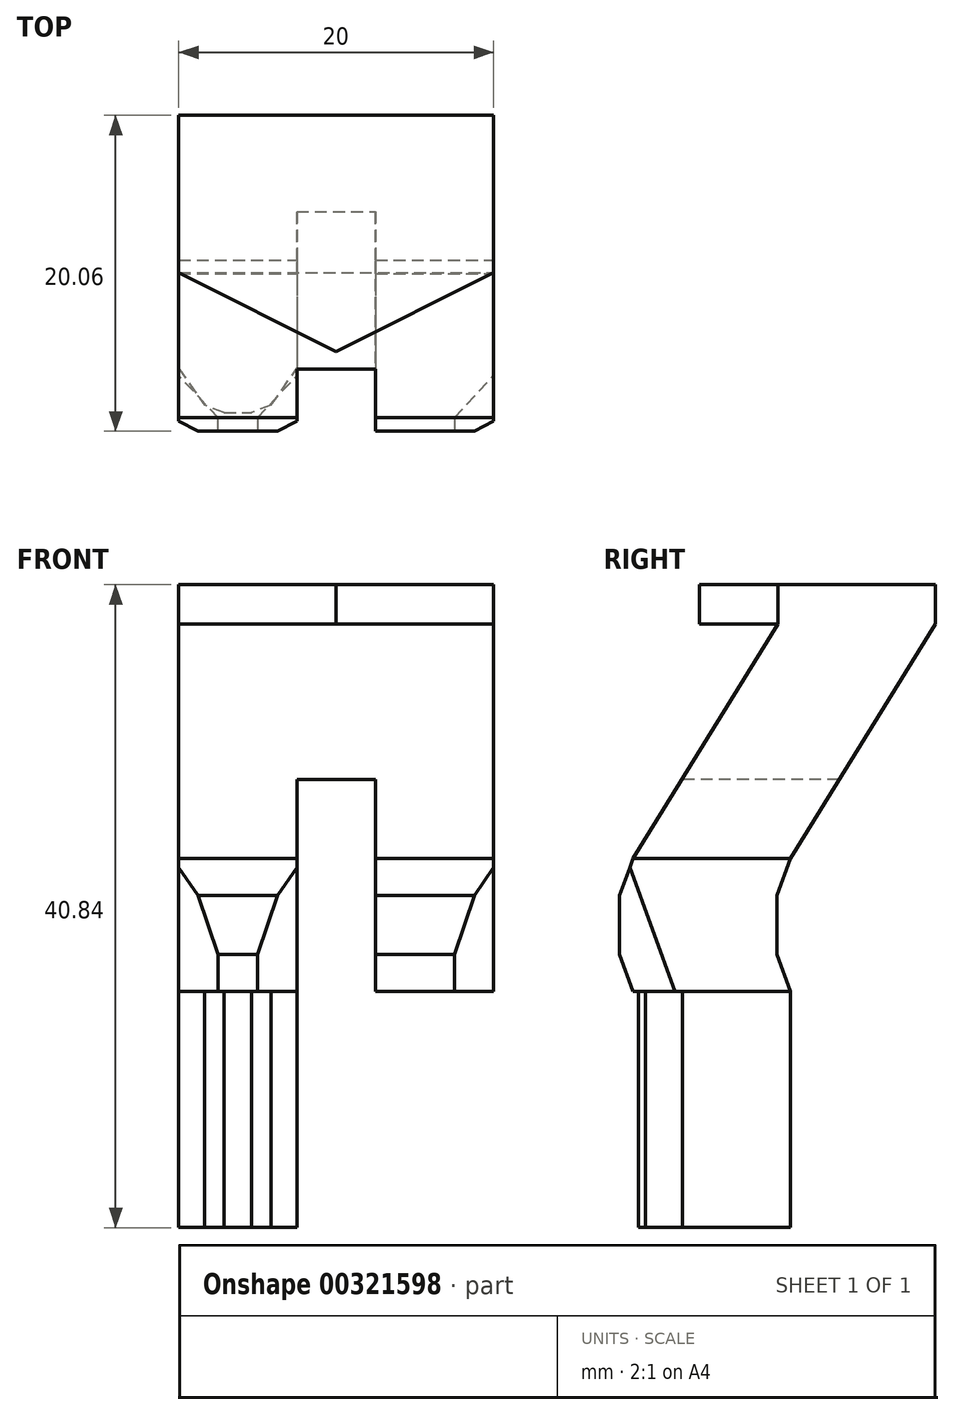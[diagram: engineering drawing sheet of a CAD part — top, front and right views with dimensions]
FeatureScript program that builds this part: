
annotation { "Feature Type Name" : "Feature", "Feature Type Description" : "" }
export const myFeature = defineFeature(function(context is Context, id is Id, definition is map)
    precondition{}
    {
        {
            var Q0;
            Q0=qCreatedBy(makeId("Top.planeOp"),FACE);
            var sketch = newSketch(context, id + "F0", { "sketchPlane" : qUnion([Q0])});
            skLineSegment(sketch, "E0", {"start": v(0, 0) * mm, "end": v(10, 0) * mm});
            skLineSegment(sketch, "E1", {"start": v(0, 0) * mm, "end": v(-10, 0) * mm});
            skLineSegment(sketch, "E2", {"start": v(-10, 0) * mm, "end": v(-10, -10) * mm});
            skLineSegment(sketch, "E3", {"start": v(10, 0) * mm, "end": v(10, -10) * mm});
            skLineSegment(sketch, "E4", {"start": v(0, 0) * mm, "end": v(0, -15) * mm});
            skLineSegment(sketch, "E5", {"start": v(-10, -10) * mm, "end": v(0, -15) * mm});
            skLineSegment(sketch, "E6", {"start": v(10, -10) * mm, "end": v(0, -15) * mm});
            skSolve(sketch);
        }
        {
            var Q0;
            Q0=makeQuery(id+"F0.imprint","IMPRINT",FACE,{"disambiguationData":[TD([[makeQuery(id+"F0.imprint","IMPRINT",EDGE,{"derivedFrom":sQuery(id+"F0.wireOp",EDGE,"E1")}),1.0]])]});
            var Q1;
            Q1=makeQuery(id+"F0.imprint","IMPRINT",FACE,{"disambiguationData":[TD([[makeQuery(id+"F0.imprint","IMPRINT",EDGE,{"derivedFrom":sQuery(id+"F0.wireOp",EDGE,"E0")}),-1.0]])]});
            extrude(context, id + "F1", {"entities" : qUnion([Q0, Q1]), "depth" : 2.5 * mm});
        }
        {
            var Q0;
            Q0=makeQuery(id+"F1.opExtrude","SWEPT_FACE",FACE,{"disambiguationData":[OSD([sQuery(id+"F0.wireOp",EDGE,"E3")])]});
            var sketch = newSketch(context, id + "F2", { "sketchPlane" : qUnion([Q0])});
            skLineSegment(sketch, "E7", {"start": v(-10, 0) * mm, "end": v(-19.2, -14.89) * mm});
            skLineSegment(sketch, "E8", {"start": v(-19.2, -14.89) * mm, "end": v(-9.2, -14.89) * mm});
            skLineSegment(sketch, "E9", {"start": v(0, 0) * mm, "end": v(-9.2, -14.89) * mm});
            skSolve(sketch);
        }
        {
            var Q0;
            Q0=makeQuery(id+"F2.imprint","IMPRINT",FACE,{"disambiguationData":[TD([[makeQuery(id+"F2.imprint","IMPRINT",EDGE,{"derivedFrom":sQuery(id+"F2.wireOp",EDGE,"E7")}),1.0]])]});
            extrude(context, id + "F3", {"entities" : qUnion([Q0]), "operationType" : NewBodyOperationType.ADD, "oppositeDirection" : true, "depth" : 20 * mm});
        }
        {
            var Q0;
            Q0=makeQuery(id+"F3.opExtrude","SWEPT_FACE",FACE,{"disambiguationData":[OSD([sQuery(id+"F2.wireOp",EDGE,"E8")])]});
            var sketch = newSketch(context, id + "F4", { "sketchPlane" : qUnion([Q0])});
            skLineSegment(sketch, "E10", {"start": v(-10, 9.2) * mm, "end": v(-2.5, 9.2) * mm});
            skLineSegment(sketch, "E11", {"start": v(10, 9.2) * mm, "end": v(2.5, 9.2) * mm});
            skLineSegment(sketch, "E12", {"start": v(-2.5, 9.2) * mm, "end": v(-2.5, 0) * mm});
            skLineSegment(sketch, "E13.bottom", {"start": v(-2.5, 0) * mm, "end": v(2.5, 0) * mm});
            skLineSegment(sketch, "E13.top", {"start": v(-2.5, 19.2) * mm, "end": v(2.5, 19.2) * mm});
            skLineSegment(sketch, "E13.left", {"start": v(-2.5, 0) * mm, "end": v(-2.5, 19.2) * mm});
            skLineSegment(sketch, "E13.right", {"start": v(2.5, 0) * mm, "end": v(2.5, 19.2) * mm});
            skSolve(sketch);
        }
        {
            var Q0;
            {var subQ0=sQuery(id+"F4.wireOp",EDGE,"E13.top");Q0=makeQuery(id+"F4.imprint","IMPRINT",FACE,{"disambiguationData":[TD([[makeQuery(id+"F4.imprint","IMPRINT",EDGE,{"derivedFrom":subQ0}),-1.0]])]});}
            var Q1;
            {var subQ0=sQuery(id+"F4.wireOp",EDGE,"E13.bottom");Q1=makeQuery(id+"F4.imprint","IMPRINT",FACE,{"disambiguationData":[TD([[makeQuery(id+"F4.imprint","IMPRINT",EDGE,{"derivedFrom":subQ0}),1.0]])]});}
            extrude(context, id + "F5", {"entities" : qUnion([Q0, Q1]), "operationType" : NewBodyOperationType.REMOVE, "oppositeDirection" : true, "depth" : 5 * mm});
        }
        {
            var Q0;
            {var subQ0=sQuery(id+"F0.wireOp",EDGE,"E3");Q0=makeQuery(id+"F3.boolean.opBoolean","MERGE",FACE,{"derivedFrom":[makeQuery(id+"F1.opExtrude","SWEPT_FACE",FACE,{"disambiguationData":[OSD([subQ0])]}),makeQuery(id+"F3.opExtrude","CAP_FACE",FACE,{"disambiguationData":[OSD([subQ0,sQuery(id+"F2.wireOp",EDGE,"E7"),sQuery(id+"F2.wireOp",EDGE,"E8"),sQuery(id+"F2.wireOp",EDGE,"E9")])],"isStart":true})]});}
            var sketch = newSketch(context, id + "F6", { "sketchPlane" : qUnion([Q0])});
            skLineSegment(sketch, "E14", {"start": v(-19.2, -14.89) * mm, "end": v(-20.06, -17.24) * mm});
            skLineSegment(sketch, "E15", {"start": v(-9.2, -14.89) * mm, "end": v(-10.06, -17.24) * mm});
            skLineSegment(sketch, "E16", {"start": v(-20.06, -17.24) * mm, "end": v(-20.06, -20.99) * mm});
            skLineSegment(sketch, "E17", {"start": v(-10.06, -17.24) * mm, "end": v(-10.06, -20.99) * mm});
            skLineSegment(sketch, "E18", {"start": v(-20.06, -20.99) * mm, "end": v(-19.2, -23.34) * mm});
            skLineSegment(sketch, "E19", {"start": v(-19.2, -23.34) * mm, "end": v(-9.2, -23.34) * mm});
            skLineSegment(sketch, "E20", {"start": v(-10.06, -20.99) * mm, "end": v(-9.2, -23.34) * mm});
            skSolve(sketch);
        }
        {
            var Q0;
            Q0=makeQuery(id+"F6.imprint","IMPRINT",FACE,{"disambiguationData":[TD([[makeQuery(id+"F6.imprint","IMPRINT",EDGE,{"derivedFrom":sQuery(id+"F6.wireOp",EDGE,"E14")}),1.0]])]});
            extrude(context, id + "F7", {"entities" : qUnion([Q0]), "oppositeDirection" : true, "depth" : 20 * mm});
        }
        {
            var Q0;
            Q0=makeQuery(id+"F7.opExtrude","SWEPT_FACE",FACE,{"disambiguationData":[OSD([sQuery(id+"F6.wireOp",EDGE,"E19")])]});
            var sketch = newSketch(context, id + "F8", { "sketchPlane" : qUnion([Q0])});
            skLineSegment(sketch, "E21", {"start": v(-10, 9.2) * mm, "end": v(-2.5, 9.2) * mm});
            skLineSegment(sketch, "E22", {"start": v(10, 9.2) * mm, "end": v(2.5, 9.2) * mm});
            skLineSegment(sketch, "E23", {"start": v(-2.5, 9.2) * mm, "end": v(-2.5, 19.96) * mm});
            skLineSegment(sketch, "E24", {"start": v(2.5, 9.2) * mm, "end": v(2.5, 20.55) * mm});
            skLineSegment(sketch, "E25.bottom", {"start": v(-2.5, 9.2) * mm, "end": v(2.5, 9.2) * mm});
            skLineSegment(sketch, "E25.top", {"start": v(-2.5, 20.09) * mm, "end": v(2.5, 20.09) * mm});
            skLineSegment(sketch, "E25.left", {"start": v(-2.5, 9.2) * mm, "end": v(-2.5, 20.09) * mm});
            skLineSegment(sketch, "E25.right", {"start": v(2.5, 9.2) * mm, "end": v(2.5, 20.09) * mm});
            skSolve(sketch);
        }
        {
            var Q0;
            {var subQ0=sQuery(id+"F8.wireOp",EDGE,"E25.top");Q0=makeQuery(id+"F8.imprint","IMPRINT",FACE,{"disambiguationData":[TD([[makeQuery(id+"F8.imprint","IMPRINT",EDGE,{"derivedFrom":subQ0}),-1.0]])]});}
            var Q1;
            {var subQ0=sQuery(id+"F8.wireOp",EDGE,"E25.bottom");Q1=makeQuery(id+"F8.imprint","IMPRINT",FACE,{"disambiguationData":[TD([[makeQuery(id+"F8.imprint","IMPRINT",EDGE,{"derivedFrom":subQ0}),1.0]])]});}
            extrude(context, id + "F9", {"entities" : qUnion([Q0, Q1]), "operationType" : NewBodyOperationType.REMOVE, "oppositeDirection" : true, "depth" : 8.45 * mm});
        }
        {
            var Q0;
            {var subQ1=sQuery(id+"F6.wireOp",EDGE,"E19");Q0=makeQuery(id+"F9.boolean.opBoolean","SPLIT",FACE,{"disambiguationData":[TD([makeQuery(id+"F9.opExtrude","SWEPT_FACE",FACE,{"disambiguationData":[OSD([sQuery(id+"F8.wireOp",EDGE,"E25.left")])]})])],"derivedFrom":makeQuery(id+"F7.opExtrude","SWEPT_FACE",FACE,{"disambiguationData":[OSD([subQ1])]})});}
            var sketch = newSketch(context, id + "F10", { "sketchPlane" : qUnion([Q0])});
            skLineSegment(sketch, "E26", {"start": v(-6.25, 19.2) * mm, "end": v(-10, 17.8) * mm});
            skLineSegment(sketch, "E27", {"start": v(-2.5, 17.8) * mm, "end": v(-6.25, 19.2) * mm});
            skLineSegment(sketch, "E28.bottom", {"start": v(-10, 17.8) * mm, "end": v(-2.5, 17.8) * mm});
            skLineSegment(sketch, "E28.top", {"start": v(-10, 9.2) * mm, "end": v(-2.5, 9.2) * mm});
            skLineSegment(sketch, "E28.left", {"start": v(-10, 17.8) * mm, "end": v(-10, 9.2) * mm});
            skLineSegment(sketch, "E28.right", {"start": v(-2.5, 17.8) * mm, "end": v(-2.5, 9.2) * mm});
            skSolve(sketch);
        }
        {
            var Q0;
            {var subQ1=sQuery(id+"F6.wireOp",EDGE,"E19");Q0=makeQuery(id+"F9.boolean.opBoolean","SPLIT",FACE,{"disambiguationData":[TD([makeQuery(id+"F9.opExtrude","SWEPT_FACE",FACE,{"disambiguationData":[OSD([sQuery(id+"F8.wireOp",EDGE,"E25.right")])]})])],"derivedFrom":makeQuery(id+"F7.opExtrude","SWEPT_FACE",FACE,{"disambiguationData":[OSD([subQ1])]})});}
            var sketch = newSketch(context, id + "F11", { "sketchPlane" : qUnion([Q0])});
            skLineSegment(sketch, "E29", {"start": v(6.25, 19.2) * mm, "end": v(2.5, 17.8) * mm});
            skLineSegment(sketch, "E30", {"start": v(10, 17.8) * mm, "end": v(6.25, 19.2) * mm});
            skLineSegment(sketch, "E31.bottom", {"start": v(2.5, 17.8) * mm, "end": v(10, 17.8) * mm});
            skLineSegment(sketch, "E31.top", {"start": v(2.5, 9.2) * mm, "end": v(10, 9.2) * mm});
            skLineSegment(sketch, "E31.left", {"start": v(2.5, 17.8) * mm, "end": v(2.5, 9.2) * mm});
            skLineSegment(sketch, "E31.right", {"start": v(10, 17.8) * mm, "end": v(10, 9.2) * mm});
            skSolve(sketch);
        }
        {
            var Q0;
            Q0=makeQuery(id+"F10.imprint","IMPRINT",FACE,{"disambiguationData":[TD([[makeQuery(id+"F10.imprint","IMPRINT",EDGE,{"derivedFrom":sQuery(id+"F10.wireOp",EDGE,"E28.bottom")}),-1.0]])]});
            var Q1;
            Q1=makeQuery(id+"F10.imprint","IMPRINT",FACE,{"disambiguationData":[TD([[makeQuery(id+"F10.imprint","IMPRINT",EDGE,{"derivedFrom":sQuery(id+"F10.wireOp",EDGE,"E26")}),1.0]])]});
            var Q2;
            Q2=makeQuery(id+"F11.imprint","IMPRINT",FACE,{"disambiguationData":[TD([[makeQuery(id+"F11.imprint","IMPRINT",EDGE,{"derivedFrom":sQuery(id+"F11.wireOp",EDGE,"E31.bottom")}),-1.0]])]});
            var Q3;
            Q3=makeQuery(id+"F11.imprint","IMPRINT",FACE,{"disambiguationData":[TD([[makeQuery(id+"F11.imprint","IMPRINT",EDGE,{"derivedFrom":sQuery(id+"F11.wireOp",EDGE,"E29")}),1.0]])]});
            extrude(context, id + "F12", {"entities" : qUnion([Q0, Q1, Q2, Q3]), "depth" : 15 * mm});
        }
        {
            var Q0;
            Q0=makeQuery(id+"F7.opExtrude","CAP_EDGE",EDGE,{"disambiguationData":[OSD([sQuery(id+"F6.wireOp",EDGE,"E18")])],"isStart":true});
            var Q1;
            Q1=makeQuery(id+"F7.opExtrude","CAP_EDGE",EDGE,{"disambiguationData":[OSD([sQuery(id+"F6.wireOp",EDGE,"E18")])],"isStart":false});
            var Q2;
            Q2=makeQuery(id+"F9.boolean.opBoolean","INTERSECT",EDGE,{"derivedFrom":[makeQuery(id+"F7.opExtrude","SWEPT_FACE",FACE,{"disambiguationData":[OSD([sQuery(id+"F6.wireOp",EDGE,"E18")])]}),makeQuery(id+"F9.opExtrude","SWEPT_FACE",FACE,{"disambiguationData":[OSD([sQuery(id+"F8.wireOp",EDGE,"E25.left")])]})]});
            var Q3;
            Q3=makeQuery(id+"F9.boolean.opBoolean","INTERSECT",EDGE,{"derivedFrom":[makeQuery(id+"F7.opExtrude","SWEPT_FACE",FACE,{"disambiguationData":[OSD([sQuery(id+"F6.wireOp",EDGE,"E18")])]}),makeQuery(id+"F9.opExtrude","SWEPT_FACE",FACE,{"disambiguationData":[OSD([sQuery(id+"F8.wireOp",EDGE,"E25.right")])]})]});
            chamfer(context, id + "F13", {"entities" : qUnion([Q0, Q1, Q2, Q3]), "width" : 2.5 * mm, "tangentPropagation" : true});
        }
        {
            var Q0;
            Q0=makeQuery(id+"F12.opExtrude","SWEPT_EDGE",EDGE,{"disambiguationData":[OSD([sQuery(id+"F6.wireOp",EDGE,"E19"),sQuery(id+"F11.wireOp",EDGE,"E30"),sQuery(id+"F11.wireOp",EDGE,"E31.bottom"),sQuery(id+"F11.wireOp",EDGE,"E31.right")])]});
            var Q1;
            Q1=makeQuery(id+"F12.opExtrude","SWEPT_EDGE",EDGE,{"disambiguationData":[OSD([sQuery(id+"F8.wireOp",EDGE,"E25.right"),sQuery(id+"F11.wireOp",EDGE,"E29"),sQuery(id+"F11.wireOp",EDGE,"E31.bottom"),sQuery(id+"F11.wireOp",EDGE,"E31.left")])]});
            var Q2;
            Q2=makeQuery(id+"F12.opExtrude","SWEPT_EDGE",EDGE,{"disambiguationData":[OSD([sQuery(id+"F6.wireOp",EDGE,"E19"),sQuery(id+"F10.wireOp",EDGE,"E26"),sQuery(id+"F10.wireOp",EDGE,"E28.bottom"),sQuery(id+"F10.wireOp",EDGE,"E28.left")])]});
            var Q3;
            Q3=makeQuery(id+"F12.opExtrude","SWEPT_EDGE",EDGE,{"disambiguationData":[OSD([sQuery(id+"F8.wireOp",EDGE,"E25.left"),sQuery(id+"F10.wireOp",EDGE,"E27"),sQuery(id+"F10.wireOp",EDGE,"E28.bottom"),sQuery(id+"F10.wireOp",EDGE,"E28.right")])]});
            chamfer(context, id + "F14", {"entities" : qUnion([Q0, Q1, Q2, Q3]), "width" : 2.5 * mm, "tangentPropagation" : true});
        }
    });
